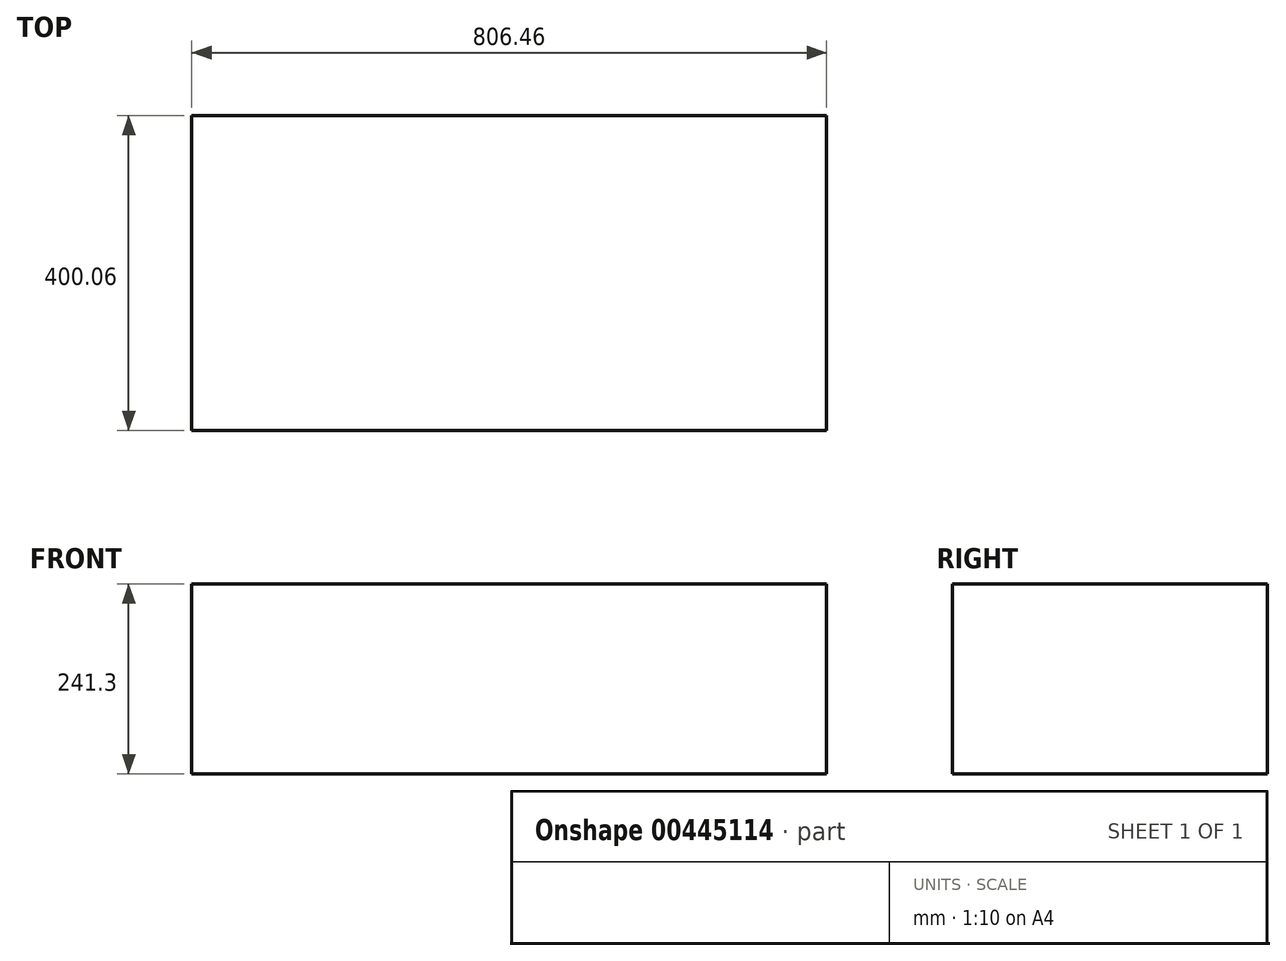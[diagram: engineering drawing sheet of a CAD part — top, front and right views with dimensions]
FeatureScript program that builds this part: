
annotation { "Feature Type Name" : "Feature", "Feature Type Description" : "" }
export const myFeature = defineFeature(function(context is Context, id is Id, definition is map)
    precondition{}
    {
        {
            var Q0;
            Q0=qCreatedBy(makeId("Top.planeOp"),FACE);
            var sketch = newSketch(context, id + "F0", { "sketchPlane" : qUnion([Q0])});
            skLineSegment(sketch, "E0.bottom", {"start": v(403.23, 200.03) * mm, "end": v(-403.22, 200.03) * mm});
            skLineSegment(sketch, "E0.top", {"start": v(403.23, -200.03) * mm, "end": v(-403.23, -200.03) * mm});
            skLineSegment(sketch, "E0.left", {"start": v(403.23, 200.03) * mm, "end": v(403.23, -200.03) * mm});
            skLineSegment(sketch, "E0.right", {"start": v(-403.23, 200.03) * mm, "end": v(-403.23, -200.03) * mm});
            skPoint(sketch, "E0.middle", {"position": v(0, 0) * mm});
            skSolve(sketch);
        }
        {
            var Q0;
            Q0 = qSketchRegion(id + "F0", true);
            extrude(context, id + "F1", {"entities" : qUnion([Q0]), "depth" : 241.3 * mm});
        }
    });
